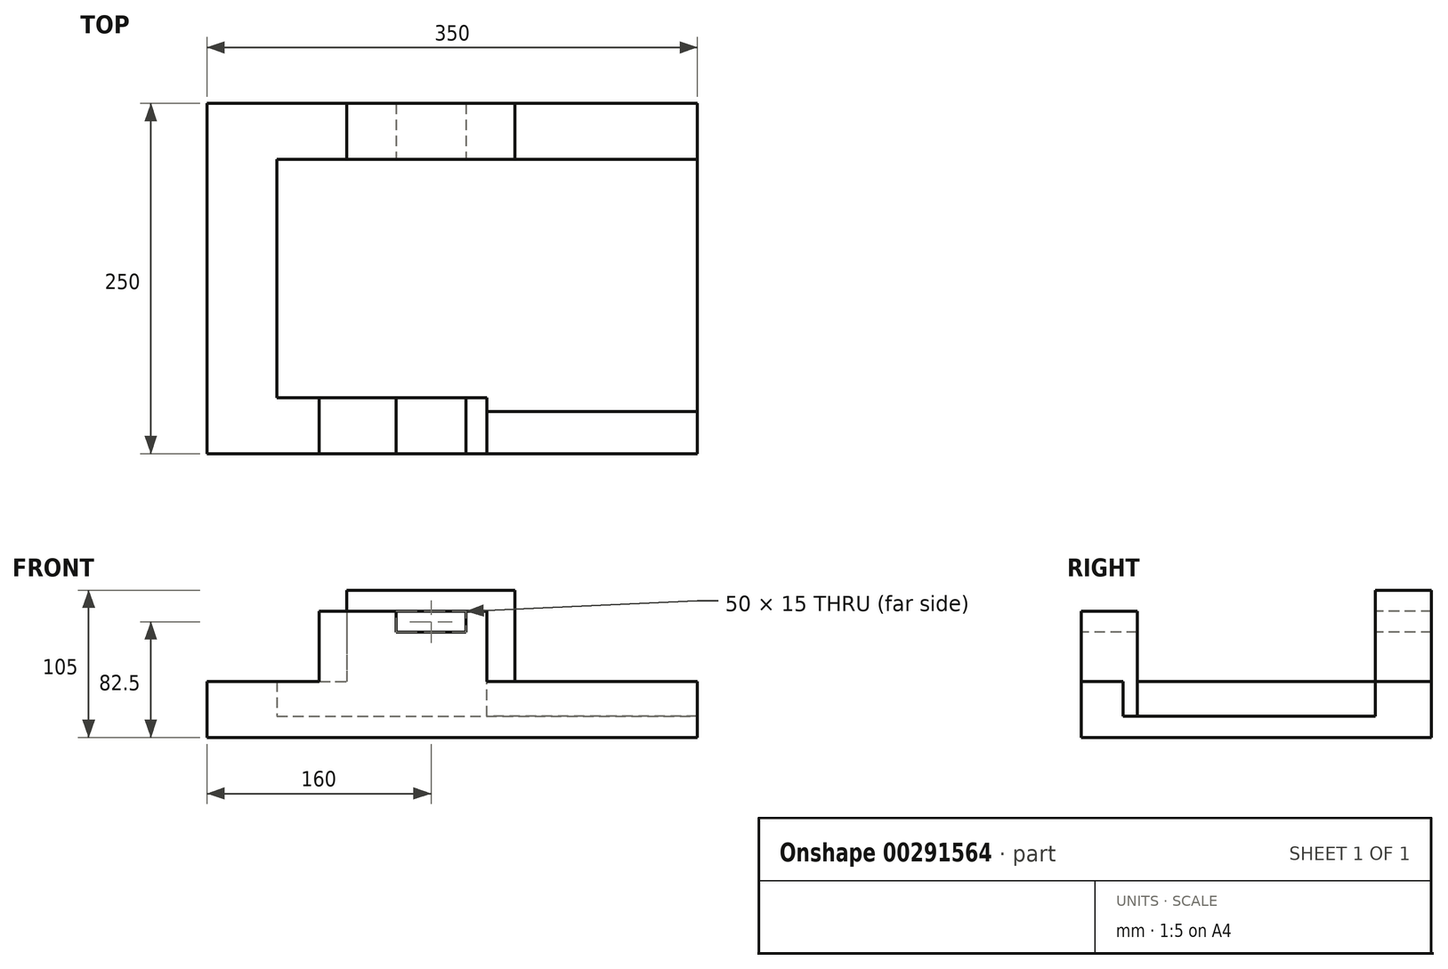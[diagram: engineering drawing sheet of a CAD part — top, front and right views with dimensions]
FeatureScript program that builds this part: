
annotation { "Feature Type Name" : "Feature", "Feature Type Description" : "" }
export const myFeature = defineFeature(function(context is Context, id is Id, definition is map)
    precondition{}
    {
        {
            var Q0;
            Q0=qCreatedBy(makeId("Top.planeOp"),FACE);
            var sketch = newSketch(context, id + "F0", { "sketchPlane" : qUnion([Q0])});
            skLineSegment(sketch, "E0.bottom", {"start": v(-175, 125) * mm, "end": v(175, 125) * mm});
            skLineSegment(sketch, "E0.top", {"start": v(-175, -125) * mm, "end": v(175, -125) * mm});
            skLineSegment(sketch, "E0.left", {"start": v(-175, 125) * mm, "end": v(-175, -125) * mm});
            skLineSegment(sketch, "E0.right", {"start": v(175, 125) * mm, "end": v(175, -125) * mm});
            skSolve(sketch);
        }
        {
            var Q0;
            Q0=makeQuery(id+"F0.imprint","IMPRINT",FACE,{"disambiguationData":[TD([[makeQuery(id+"F0.imprint","IMPRINT",EDGE,{"derivedFrom":sQuery(id+"F0.wireOp",EDGE,"E0.bottom")}),-1.0]])]});
            extrude(context, id + "F1", {"entities" : qUnion([Q0]), "depth" : 40 * mm});
        }
        {
            var Q0;
            Q0=makeQuery(id+"F1.opExtrude","SWEPT_FACE",FACE,{"disambiguationData":[OSD([sQuery(id+"F0.wireOp",EDGE,"E0.right")])]});
            var sketch = newSketch(context, id + "F2", { "sketchPlane" : qUnion([Q0])});
            skLineSegment(sketch, "E1.bottom", {"start": v(-85, 40) * mm, "end": v(85, 40) * mm});
            skLineSegment(sketch, "E1.top", {"start": v(-85, 15) * mm, "end": v(85, 15) * mm});
            skLineSegment(sketch, "E1.left", {"start": v(-85, 40) * mm, "end": v(-85, 15) * mm});
            skLineSegment(sketch, "E1.right", {"start": v(85, 40) * mm, "end": v(85, 15) * mm});
            skSolve(sketch);
        }
        {
            var Q0;
            Q0=makeQuery(id+"F2.imprint","IMPRINT",FACE,{"disambiguationData":[TD([[makeQuery(id+"F2.imprint","IMPRINT",EDGE,{"derivedFrom":sQuery(id+"F2.wireOp",EDGE,"E1.bottom")}),-1.0]])]});
            var Q1;
            Q1=makeQuery(id+"F2.imprint","IMPRINT",FACE,{"disambiguationData":[TD([[makeQuery(id+"F2.imprint","IMPRINT",EDGE,{"derivedFrom":sQuery(id+"F2.wireOp",EDGE,"E1.bottom")}),1.0]])]});
            extrude(context, id + "F3", {"entities" : qUnion([Q0, Q1]), "operationType" : NewBodyOperationType.REMOVE, "oppositeDirection" : true, "depth" : 300 * mm});
        }
        {
            var Q0;
            Q0=makeQuery(id+"F1.opExtrude","CAP_FACE",FACE,{"disambiguationData":[OSD([sQuery(id+"F0.wireOp",EDGE,"E0.bottom"),sQuery(id+"F0.wireOp",EDGE,"E0.top"),sQuery(id+"F0.wireOp",EDGE,"E0.left"),sQuery(id+"F0.wireOp",EDGE,"E0.right")])],"isStart":false});
            var sketch = newSketch(context, id + "F4", { "sketchPlane" : qUnion([Q0])});
            skLineSegment(sketch, "E2.bottom", {"start": v(175, -85) * mm, "end": v(25, -85) * mm});
            skLineSegment(sketch, "E2.top", {"start": v(175, -95) * mm, "end": v(25, -95) * mm});
            skLineSegment(sketch, "E2.left", {"start": v(175, -85) * mm, "end": v(175, -95) * mm});
            skLineSegment(sketch, "E2.right", {"start": v(25, -85) * mm, "end": v(25, -95) * mm});
            skSolve(sketch);
        }
        {
            var Q0;
            Q0=makeQuery(id+"F4.imprint","IMPRINT",FACE,{"disambiguationData":[TD([[makeQuery(id+"F4.imprint","IMPRINT",EDGE,{"derivedFrom":sQuery(id+"F4.wireOp",EDGE,"E2.bottom")}),-1.0]])]});
            extrude(context, id + "F5", {"entities" : qUnion([Q0]), "operationType" : NewBodyOperationType.REMOVE, "oppositeDirection" : true, "depth" : 25 * mm});
        }
        {
            var Q0;
            Q0=makeQuery(id+"F1.opExtrude","CAP_FACE",FACE,{"disambiguationData":[OSD([sQuery(id+"F0.wireOp",EDGE,"E0.bottom"),sQuery(id+"F0.wireOp",EDGE,"E0.top"),sQuery(id+"F0.wireOp",EDGE,"E0.left"),sQuery(id+"F0.wireOp",EDGE,"E0.right")])],"isStart":false});
            var sketch = newSketch(context, id + "F6", { "sketchPlane" : qUnion([Q0])});
            skLineSegment(sketch, "E3.bottom", {"start": v(25, -85) * mm, "end": v(-95, -85) * mm});
            skLineSegment(sketch, "E3.top", {"start": v(25, -125) * mm, "end": v(-95, -125) * mm});
            skLineSegment(sketch, "E3.left", {"start": v(25, -85) * mm, "end": v(25, -125) * mm});
            skLineSegment(sketch, "E3.right", {"start": v(-95, -85) * mm, "end": v(-95, -125) * mm});
            skSolve(sketch);
        }
        {
            var Q0;
            {var subQ3=sQuery(id+"F6.wireOp",EDGE,"E3.bottom");Q0=makeQuery(id+"F6.imprint","IMPRINT",FACE,{"disambiguationData":[TD([[makeQuery(id+"F6.imprint","IMPRINT",EDGE,{"derivedFrom":subQ3}),-1.0]])]});}
            extrude(context, id + "F7", {"entities" : qUnion([Q0]), "operationType" : NewBodyOperationType.ADD, "depth" : 50 * mm});
        }
        {
            var Q0;
            {var subQ0=sQuery(id+"F0.wireOp",EDGE,"E0.left");var subQ1=sQuery(id+"F0.wireOp",EDGE,"E0.top");var subQ2=sQuery(id+"F0.wireOp",EDGE,"E0.right");var subQ5=sQuery(id+"F0.wireOp",EDGE,"E0.bottom");Q0=makeQuery(id+"F7.boolean.opBoolean","SPLIT",FACE,{"disambiguationData":[TD([makeQuery(id+"F1.opExtrude","SWEPT_FACE",FACE,{"disambiguationData":[OSD([subQ5])]})])],"derivedFrom":makeQuery(id+"F1.opExtrude","CAP_FACE",FACE,{"disambiguationData":[OSD([subQ5,subQ1,subQ0,subQ2])],"isStart":false})});}
            var sketch = newSketch(context, id + "F8", { "sketchPlane" : qUnion([Q0])});
            skLineSegment(sketch, "E4.bottom", {"start": v(-75, 125) * mm, "end": v(45, 125) * mm});
            skLineSegment(sketch, "E4.top", {"start": v(-75, 85) * mm, "end": v(45, 85) * mm});
            skLineSegment(sketch, "E4.left", {"start": v(-75, 125) * mm, "end": v(-75, 85) * mm});
            skLineSegment(sketch, "E4.right", {"start": v(45, 125) * mm, "end": v(45, 85) * mm});
            skSolve(sketch);
        }
        {
            var Q0;
            Q0=makeQuery(id+"F8.imprint","IMPRINT",FACE,{"disambiguationData":[TD([[makeQuery(id+"F8.imprint","IMPRINT",EDGE,{"derivedFrom":sQuery(id+"F8.wireOp",EDGE,"E4.bottom")}),-1.0]])]});
            extrude(context, id + "F9", {"entities" : qUnion([Q0]), "operationType" : NewBodyOperationType.ADD, "depth" : 65 * mm});
        }
        {
            var Q0;
            Q0=makeQuery(id+"F7.boolean.opBoolean","MERGE",FACE,{"derivedFrom":[makeQuery(id+"F1.opExtrude","SWEPT_FACE",FACE,{"disambiguationData":[OSD([sQuery(id+"F0.wireOp",EDGE,"E0.top")])]}),makeQuery(id+"F7.opExtrude","SWEPT_FACE",FACE,{"disambiguationData":[OSD([sQuery(id+"F6.wireOp",EDGE,"E3.top")])]})]});
            var sketch = newSketch(context, id + "F10", { "sketchPlane" : qUnion([Q0])});
            skLineSegment(sketch, "E5.bottom", {"start": v(-40, 90) * mm, "end": v(10, 90) * mm});
            skLineSegment(sketch, "E5.top", {"start": v(-40, 75) * mm, "end": v(10, 75) * mm});
            skLineSegment(sketch, "E5.left", {"start": v(-40, 90) * mm, "end": v(-40, 75) * mm});
            skLineSegment(sketch, "E5.right", {"start": v(10, 90) * mm, "end": v(10, 75) * mm});
            skSolve(sketch);
        }
        {
            var Q0;
            Q0 = qSketchRegion(id + "F10", true);
            extrude(context, id + "F11", {"entities" : qUnion([Q0]), "operationType" : NewBodyOperationType.REMOVE, "endBound" : BoundingType.THROUGH_ALL, "oppositeDirection" : true, "depth" : 25 * mm});
        }
    });
